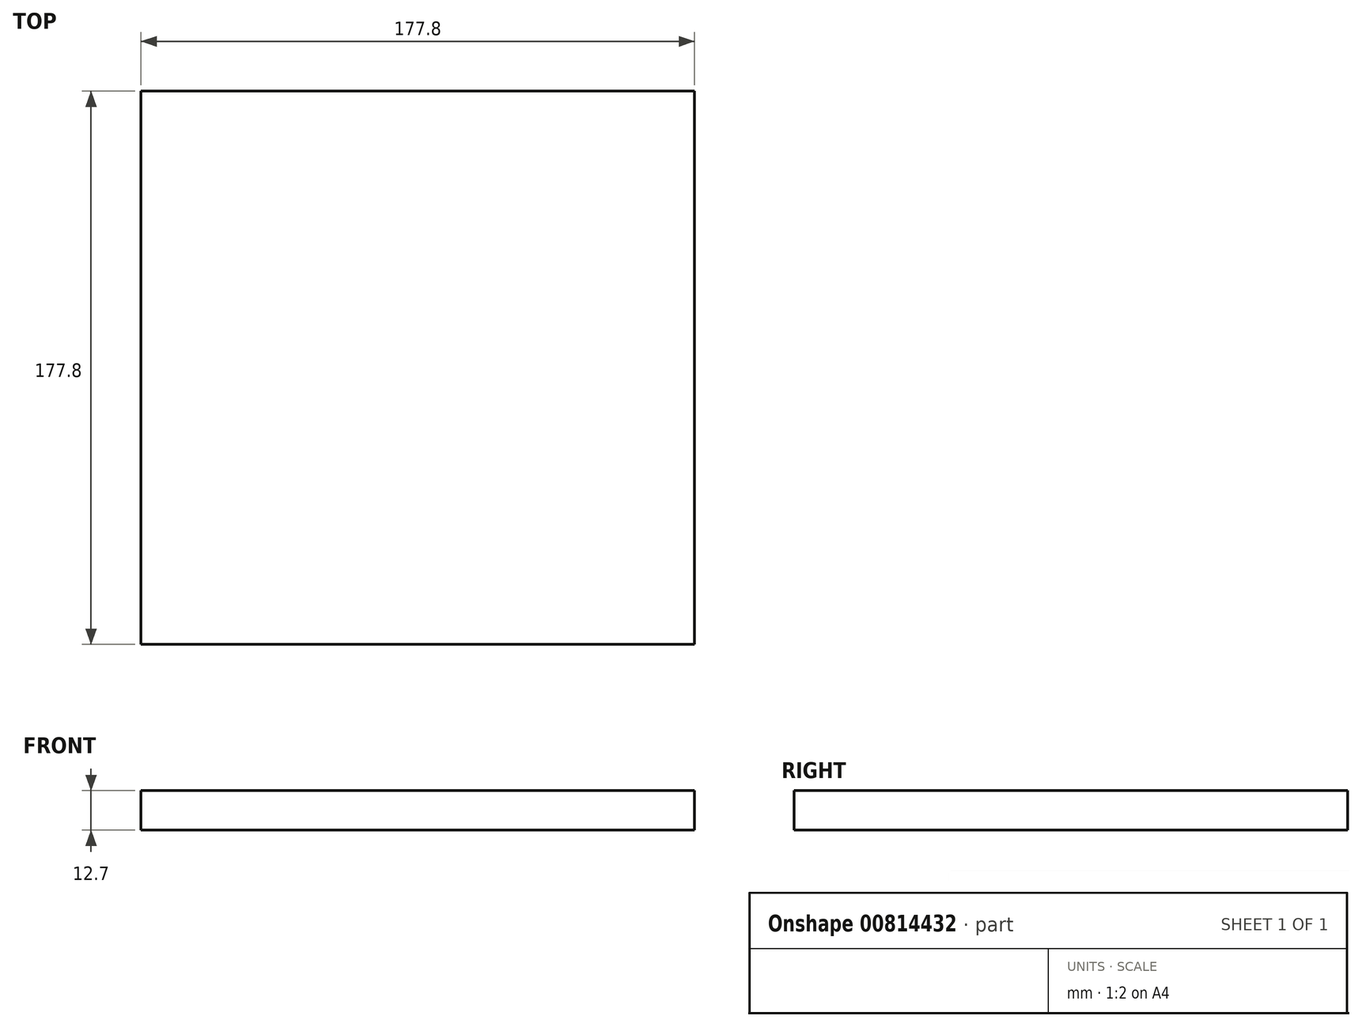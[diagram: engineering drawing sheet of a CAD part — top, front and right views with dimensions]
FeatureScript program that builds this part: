
annotation { "Feature Type Name" : "Feature", "Feature Type Description" : "" }
export const myFeature = defineFeature(function(context is Context, id is Id, definition is map)
    precondition{}
    {
        {
            var Q0;
            Q0=qCreatedBy(makeId("Top.planeOp"),FACE);
            var sketch = newSketch(context, id + "F0", { "sketchPlane" : qUnion([Q0])});
            skLineSegment(sketch, "E0.bottom", {"start": v(-154.18, 92.54) * mm, "end": v(23.62, 92.54) * mm});
            skLineSegment(sketch, "E0.top", {"start": v(-154.18, -85.26) * mm, "end": v(23.62, -85.26) * mm});
            skLineSegment(sketch, "E0.left", {"start": v(-154.18, 92.54) * mm, "end": v(-154.18, -85.26) * mm});
            skLineSegment(sketch, "E0.right", {"start": v(23.62, 92.54) * mm, "end": v(23.62, -85.26) * mm});
            skSolve(sketch);
        }
        {
            var Q0;
            Q0=makeQuery(id+"F0.imprint","IMPRINT",FACE,{"disambiguationData":[TD([[makeQuery(id+"F0.imprint","IMPRINT",EDGE,{"derivedFrom":sQuery(id+"F0.wireOp",EDGE,"E0.bottom")}),-1.0]])]});
            extrude(context, id + "F1", {"entities" : qUnion([Q0]), "depth" : 12.7 * mm, "offsetDistance" : 25.4 * mm});
        }
    });
